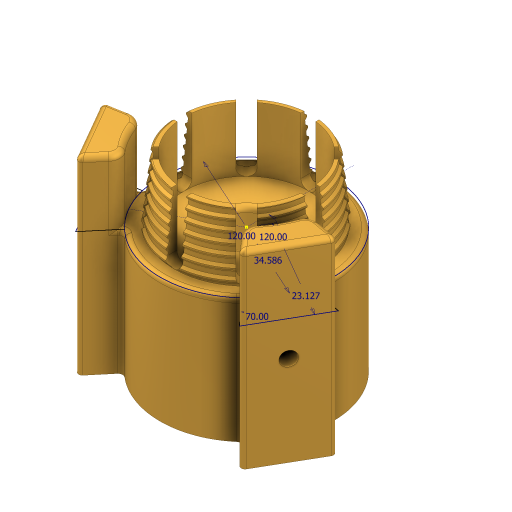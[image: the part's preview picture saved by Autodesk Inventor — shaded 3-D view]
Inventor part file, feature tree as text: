
AUTODESK INVENTOR PART (.ipt)
format: ipt  version: 2023 (Build 270158000, 158)  size: 3,042,304 bytes
history: native  units: mm
features: sketch x9, fillet x8, extrude x7, hole x3, draft x2, helix x2, direct_edit x1, pattern_circular x1, chamfer x1, other x1
ambient origin geometry x8: Origin, YZ Plane, XZ Plane, XY Plane, X Axis, Y Axis, Z Axis, Center Point
bodies: Solid1 (feature_tree)
feature tree (35):
  extrude  "Extrusion1"  Depth=26.5mm
  draft  "FaceDraft1"
  sketch  "Sketch2"  dims[d34=0.0mm d35=0.0mm d56=8.726646mm]
  helix  "Coil3"  [1 undecoded]
  helix  "Coil4"  [1 undecoded]
  direct_edit  "Direct Edit2"
  extrude  "Extrusion2"  Depth=8.726646mm
  extrude  "Extrusion13"  TaperAngle=90.0deg  [1 undecoded]
  extrude  "Extrusion14"  Depth=34.58632mm
  extrude  "Extrusion15"  TaperAngle=120.0deg  [1 undecoded]
  fillet  "Fillet10"  Radius=23.127mm
  extrude  "Extrusion16"  Depth=25.0mm TaperAngle=0.0deg
  pattern_circular  "Circular Pattern3"  Count=8 Angle=360.0deg
  hole  "Hole3"  [1 undecoded]
  hole  "Hole4"  [1 undecoded]
  fillet  "Fillet11"  Radius=1.5mm
  fillet  "Fillet12"  Radius=12.0mm
  fillet  "Fillet13"  Radius=2.5mm
  extrude  "Extrusion18"  Depth=1.0mm
  draft  "FaceDraft6"
  chamfer  "Chamfer3"  Distance=7.0mm
  fillet  "Fillet16"  Radius=10.0mm
  hole  "Hole6"  [1 undecoded]
  fillet  "Fillet17"  Radius=5.0mm
  fillet  "Fillet18"  [1 undecoded]
  fillet  "Fillet19"  Radius=2.0mm
  sketch  "Sketch1"  dims[d0=25.0mm d1=26.5mm d2=12.875mm d3=0.0mm d4=1.047198mm]
  sketch  "Sketch3"  dims[d62=2.0mm d63=13.0mm d64=10.0mm d65=1.047198mm]
  sketch  "Sketch11"  dims[d66=90.0deg d67=90.0deg d68=0.0mm d69=0.0mm d70=2.0mm d71=3.0mm d72=10.0mm d73=-1.047198mm d74=90.0deg d75=90.0deg d76=0.0mm d77=0.0mm]
  sketch  "Sketch13"  dims[d79=-0.127mm d145=34.58632mm]
  sketch  "Sketch14"  dims[d150=120.0deg d151=120.0deg d153=23.127mm]
  sketch  "Sketch16"  dims[d154=12.217305mm d157=25.0mm d158=0.0mm]
  sketch  "Sketch19"  dims[d159=3.0mm d160=80.0mm d162=360.0deg]
  sketch  "Sketch20"  dims[d164=0.0mm d165=0.0mm d166=1.0mm d179=5.3mm d180=6.0mm d181=4.0mm d182=2.0mm d183=90.0deg d184=5.0mm d185=0.0mm d186=10.0mm d187=6.0mm d188=4.0mm d189=2.0mm d190=90.0deg d191=15.0mm d192=0.0mm d193=1.0mm d194=1.5mm d195=12.0mm d196=0.0mm d197=2.5mm d208=2.9mm d209=7.0mm d210=10.0mm d211=0.0mm d212=20.0mm d213=120.0deg d223=6.0mm d224=5.5mm d225=0.0mm d226=0.0mm d227=10.0mm d228=5.0mm d229=0.0mm d230=-4.363323mm d231=0.33mm d232=2.0mm d233=45.0deg d234=0.75mm d235=5.3mm d236=6.0mm d237=20.0mm d238=2.0mm d239=90.0deg d240=10.0mm d241=0.0mm d242=0.75mm d243=1.0mm d244=1.0mm d109=0.5mm d110=0.872665mm d111=0.5mm d112=0.872665mm d245=0.0mm]
  other  "Size2"
note: 8 required parameter values undecoded (feature->parameter linkage not recoverable at this tier; creation-order binding heuristic only, values carry confidence <= 0.55)
